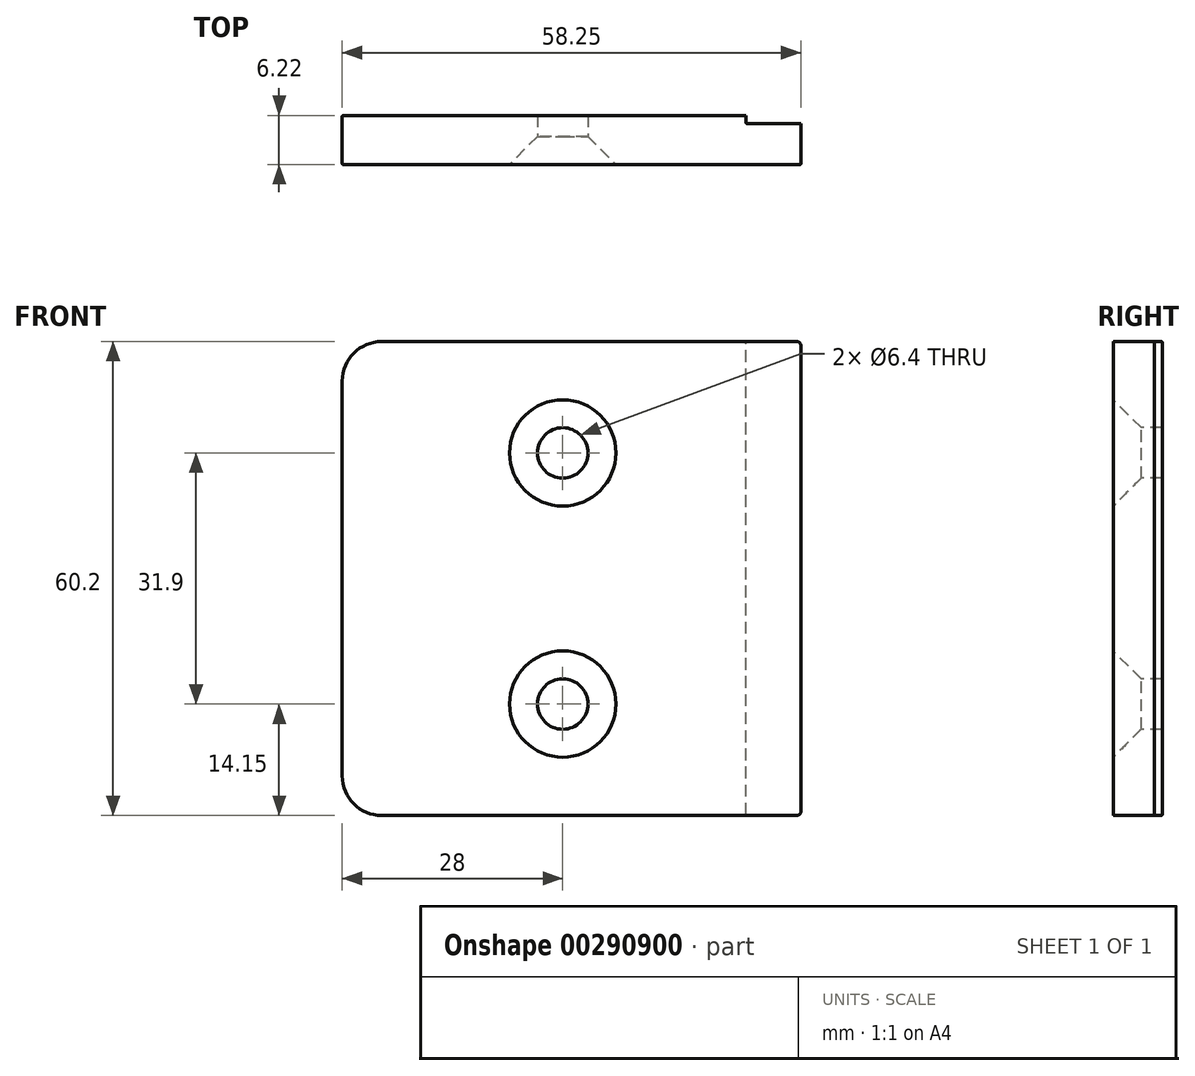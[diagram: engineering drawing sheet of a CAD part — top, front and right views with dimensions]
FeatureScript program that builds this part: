
annotation { "Feature Type Name" : "Feature", "Feature Type Description" : "" }
export const myFeature = defineFeature(function(context is Context, id is Id, definition is map)
    precondition{}
    {
        {
            var Q0;
            Q0=qCreatedBy(makeId("Front.planeOp"),FACE);
            var sketch = newSketch(context, id + "F0", { "sketchPlane" : qUnion([Q0])});
            skLineSegment(sketch, "E0.bottom", {"start": v(-0.5, 0) * mm, "end": v(-53.25, 0) * mm});
            skLineSegment(sketch, "E0.top", {"start": v(-0.5, 60.2) * mm, "end": v(-53.25, 60.2) * mm});
            skLineSegment(sketch, "E0.left", {"start": v(0, 0.5) * mm, "end": v(0, 59.7) * mm});
            skLineSegment(sketch, "E0.right", {"start": v(-58.25, 5) * mm, "end": v(-58.25, 55.2) * mm});
            skPoint(sketch, "E1.visualSharp", {"position": v(-58.25, 60.2) * mm});
            skArc(sketch, "E1.filletArc", {"start": v(-53.25, 60.2) * mm, "mid": v(-56.79, 58.74) * mm, "end": v(-58.25, 55.2) * mm});
            skPoint(sketch, "E2.visualSharp", {"position": v(-58.25, 0) * mm});
            skArc(sketch, "E2.filletArc", {"start": v(-58.25, 5) * mm, "mid": v(-56.79, 1.46) * mm, "end": v(-53.25, 0) * mm});
            skPoint(sketch, "E3.visualSharp", {"position": v(0, 0) * mm});
            skArc(sketch, "E3.filletArc", {"start": v(-0.5, 0) * mm, "mid": v(-0.15, 0.15) * mm, "end": v(0, 0.5) * mm});
            skPoint(sketch, "E4.visualSharp", {"position": v(0, 60.2) * mm});
            skArc(sketch, "E4.filletArc", {"start": v(0, 59.7) * mm, "mid": v(-0.15, 60.05) * mm, "end": v(-0.5, 60.2) * mm});
            skSolve(sketch);
        }
        {
            var Q0;
            Q0=makeQuery(id+"F0.imprint","IMPRINT",FACE,{"disambiguationData":[TD([[makeQuery(id+"F0.imprint","IMPRINT",EDGE,{"derivedFrom":sQuery(id+"F0.wireOp",EDGE,"E0.bottom")}),-1.0]])]});
            extrude(context, id + "F1", {"entities" : qUnion([Q0]), "depth" : 6.22 * mm});
        }
        {
            var Q0;
            Q0=makeQuery(id+"F1.opExtrude","SWEPT_FACE",FACE,{"disambiguationData":[OSD([sQuery(id+"F0.wireOp",EDGE,"E0.top")])]});
            var sketch = newSketch(context, id + "F2", { "sketchPlane" : qUnion([Q0])});
            skLineSegment(sketch, "E5.bottom", {"start": v(0, 0) * mm, "end": v(-7, 0) * mm});
            skLineSegment(sketch, "E5.top", {"start": v(0, -1) * mm, "end": v(-7, -1) * mm});
            skLineSegment(sketch, "E5.left", {"start": v(0, 0) * mm, "end": v(0, -1) * mm});
            skLineSegment(sketch, "E5.right", {"start": v(-7, 0) * mm, "end": v(-7, -1) * mm});
            skSolve(sketch);
        }
        {
            var Q0;
            Q0=qSketchRegion(id+"F2",true);
            extrude(context, id + "F3", {"entities" : qUnion([Q0]), "operationType" : NewBodyOperationType.REMOVE, "endBound" : BoundingType.THROUGH_ALL, "oppositeDirection" : true, "depth" : 25 * mm});
        }
        {
            var Q0;
            Q0=makeQuery(id+"F1.opExtrude","CAP_EDGE",EDGE,{"disambiguationData":[OSD([sQuery(id+"F0.wireOp",EDGE,"E0.top")])],"isStart":false});
            var Q1;
            Q1=makeQuery(id+"F1.opExtrude","CAP_EDGE",EDGE,{"disambiguationData":[OSD([sQuery(id+"F0.wireOp",EDGE,"E0.top")])],"isStart":true});
            var Q2;
            Q2=makeQuery(id+"F3.boolean.opBoolean","COPY",EDGE,{"derivedFrom":makeQuery(id+"F3.opExtrude","SWEPT_EDGE",EDGE,{"disambiguationData":[OSD([sQuery(id+"F0.wireOp",EDGE,"E0.top"),sQuery(id+"F2.wireOp",EDGE,"E5.bottom"),sQuery(id+"F2.wireOp",EDGE,"E5.right")])]})});
            var Q3;
            Q3=makeQuery(id+"F3.boolean.opBoolean","COPY",EDGE,{"derivedFrom":makeQuery(id+"F3.opExtrude","CAP_EDGE",EDGE,{"disambiguationData":[OSD([sQuery(id+"F2.wireOp",EDGE,"E5.top")])],"isStart":true})});
            var Q4;
            Q4=makeQuery(id+"F3.boolean.opBoolean","COPY",EDGE,{"derivedFrom":makeQuery(id+"F3.opExtrude","CAP_EDGE",EDGE,{"disambiguationData":[OSD([sQuery(id+"F2.wireOp",EDGE,"E5.right")])],"isStart":true})});
            var Q5;
            Q5=makeQuery(id+"F3.boolean.opBoolean","INTERSECT",EDGE,{"derivedFrom":[makeQuery(id+"F1.opExtrude","SWEPT_FACE",FACE,{"disambiguationData":[OSD([sQuery(id+"F0.wireOp",EDGE,"E0.bottom")])]}),makeQuery(id+"F3.opExtrude","SWEPT_FACE",FACE,{"disambiguationData":[OSD([sQuery(id+"F2.wireOp",EDGE,"E5.right")])]})]});
            var Q6;
            Q6=makeQuery(id+"F3.boolean.opBoolean","COPY",EDGE,{"derivedFrom":makeQuery(id+"F3.opExtrude","SWEPT_EDGE",EDGE,{"disambiguationData":[OSD([sQuery(id+"F2.wireOp",EDGE,"E5.top"),sQuery(id+"F2.wireOp",EDGE,"E5.right")])]})});
            fillet(context, id + "F4", {"entities" : qUnion([Q0, Q1, Q2, Q3, Q4, Q5, Q6]), "radius" : 0.1 * mm, "tangentPropagation" : true, "allowEdgeOverflow" : false});
        }
        {
            var Q0;
            Q0=makeQuery(id+"F1.opExtrude","CAP_FACE",FACE,{"disambiguationData":[OSD([sQuery(id+"F0.wireOp",EDGE,"E0.bottom"),sQuery(id+"F0.wireOp",EDGE,"E0.top"),sQuery(id+"F0.wireOp",EDGE,"E0.left"),sQuery(id+"F0.wireOp",EDGE,"E0.right"),sQuery(id+"F0.wireOp",EDGE,"E1.filletArc"),sQuery(id+"F0.wireOp",EDGE,"E2.filletArc"),sQuery(id+"F0.wireOp",EDGE,"E3.filletArc"),sQuery(id+"F0.wireOp",EDGE,"E4.filletArc")])],"isStart":false});
            var sketch = newSketch(context, id + "F5", { "sketchPlane" : qUnion([Q0])});
            skCircle(sketch, "E6", {"center": v(-30.25, 46.05) * mm, "radius": 3 * mm});
            skCircle(sketch, "E7.MirrorC", {"center": v(-30.25, 14.15) * mm, "radius": 3 * mm});
            skSolve(sketch);
        }
        {
            var Q0;
            Q0=sQuery(id+"F5.wireOp",VERTEX,"E6.center");
            var Q1;
            Q1=sQuery(id+"F5.wireOp",VERTEX,"E7.MirrorC.center");
            var Q2;
            Q2=makeQuery(id+"F1.opExtrude","SWEPT_BODY",BODY,{"disambiguationData":[OSD([sQuery(id+"F0.wireOp",EDGE,"E0.bottom"),sQuery(id+"F0.wireOp",EDGE,"E0.top"),sQuery(id+"F0.wireOp",EDGE,"E0.left"),sQuery(id+"F0.wireOp",EDGE,"E0.right"),sQuery(id+"F0.wireOp",EDGE,"E1.filletArc"),sQuery(id+"F0.wireOp",EDGE,"E2.filletArc"),sQuery(id+"F0.wireOp",EDGE,"E3.filletArc"),sQuery(id+"F0.wireOp",EDGE,"E4.filletArc")])]});
            hole(context, id + "F6", {"style" : HoleStyle.C_SINK, "endStyle" : HoleEndStyle.THROUGH, "holeDiameter" : 6.4 * mm, "cSinkDiameter" : 13.5 * mm, "cSinkAngle" : 90 * degree, "tappedDepth" : 10 * mm, "tapClearance" : 3, "locations" : qUnion([Q0, Q1]), "scope" : qUnion([Q2])});
        }
    });
